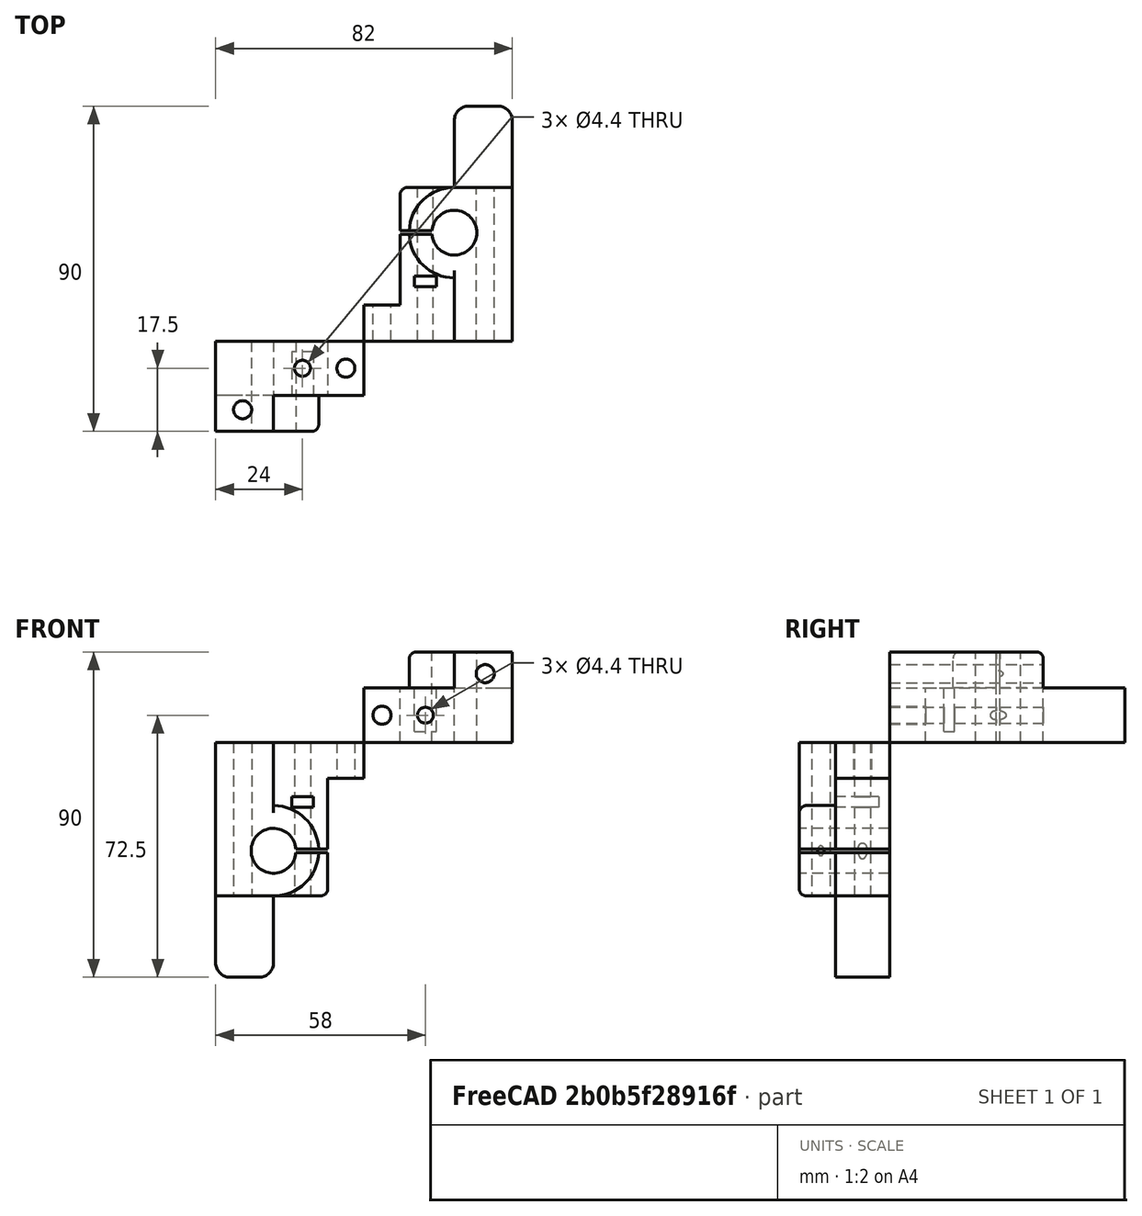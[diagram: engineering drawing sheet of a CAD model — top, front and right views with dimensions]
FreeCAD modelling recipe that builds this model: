
FCSTD DOCUMENT  (FreeCAD 0.15R4664 (Git))
Label: foot_L
License: All rights reserved
LicenseURL: http://en.wikipedia.org/wiki/All_rights_reserved
objects: Part::Box×6, Part::Cut×6, Part::Cylinder×5, Part::Fillet×4, Part::Feature×3, Part::MultiFuse×3, Mesh::Feature×1
note: 27 computed .brp shape members not serialized (recipe doc carries the construction recipe); baked Part::Feature solids carry a one-line shape summary decoded from their .brp

FEATURE [Mesh::Feature] footL_12mm
FEATURE [Part::Feature] footL_12mm001001  label="footL_12mm002"
  shape: bbox 41 x 65 x 25 mm, 3230 faces, 0 solids (baked)
FEATURE [Part::Box] Box  label="Cubo"
  Height = 15
  Length = 41
  Width = 65
FEATURE [Part::Box] Box001  label="Cubo001"
  Height = 10
  Length = 16
  Placement = pos=(25,0,15) rot=(0,0,1;0rad)
  Width = 42.5
FEATURE [Part::Cylinder] Cylinder  label="Cilindro"
  Angle = 360
  Height = 10
  Placement = pos=(25,30,15) rot=(0,0,1;0rad)
  Radius = 12.5
FEATURE [Part::Box] Box002  label="Cubo002"
  Height = 15
  Length = 10
  Placement = pos=(0,10,0) rot=(0,0,1;0rad)
  Width = 55
FEATURE [Part::Box] Box003  label="Cubo003"
  Height = 15
  Length = 15
  Placement = pos=(10,42.5,0) rot=(0,0,1;0rad)
  Width = 22.5
FEATURE [Part::Box] Box004  label="Cubo004"
  Height = 30
  Length = 25
  Placement = pos=(0,29.5,-2) rot=(0,0,1;0rad)
  Width = 1
FEATURE [Part::Box] Box005  label="Cubo005"
  Height = 17
  Length = 6
  Placement = pos=(14,15,3) rot=(0,0,1;0rad)
  Width = 3
FEATURE [Part::Cylinder] Cylinder001  label="Cilindro001"
  Angle = 360
  Height = 32
  Placement = pos=(25,30,-4) rot=(0,0,1;0rad)
  Radius = 6.2
FEATURE [Part::Cylinder] Cylinder002  label="Cilindro002"
  Angle = 360
  Height = 45
  Placement = pos=(33.55,-1,19) rot=(-1,0,0;1.5708rad)
  Radius = 2.5
FEATURE [Part::Cylinder] Cylinder003  label="Cilindro003"
  Angle = 360
  Height = 45
  Placement = pos=(17,-1,7.5) rot=(-1,0,0;1.5708rad)
  Radius = 2.2
FEATURE [Part::Cylinder] Cylinder004  label="Cilindro004"
  Angle = 360
  Height = 12
  Placement = pos=(5,-1,7.5) rot=(-1,0,0;1.5708rad)
  Radius = 2.5
FEATURE [Part::Cut] Cut
  Base = -> Box
  Tool = -> Box002
FEATURE [Part::MultiFuse] Fusion
  Shapes = -> [Cut,Box001]
FEATURE [Part::MultiFuse] Fusion001
  Shapes = -> [Fusion,Cylinder]
FEATURE [Part::Cut] Cut001
  Base = -> Fusion001
  Tool = -> Box003
FEATURE [Part::MultiFuse] Fusion002
  Shapes = -> [Cylinder004,Cylinder002,Cylinder003]
FEATURE [Part::Cut] Cut002
  Base = -> Cut001
  Tool = -> Fusion002
FEATURE [Part::Cut] Cut003
  Base = -> Cut002
  Tool = -> Cylinder001
FEATURE [Part::Cut] Cut004
  Base = -> Cut003
  Tool = -> Box005
FEATURE [Part::Cut] Cut005
  Base = -> Cut004
  Tool = -> Box004
FEATURE [Part::Fillet] Fillet
  Base = -> Cut005
  Edges = 1 edges r=2: [Edge35]
FEATURE [Part::Fillet] Fillet001
  Base = -> Fillet
  Edges = 1 edges r=2: [Edge9]
FEATURE [Part::Fillet] Fillet002
  Base = -> Fillet001
  Edges = 1 edges r=2: [Edge65]
FEATURE [Part::Fillet] Fillet003
  Base = -> Fillet002
  Edges = 2 edges r=4: [Edge51,Edge61]
FEATURE [Part::Feature] Fillet003_solid  label="Fillet003 (Solid)"
  shape: bbox 41 x 65 x 25 mm, 38 faces (baked)
FEATURE [Part::Feature] Fillet003_solid001  label="Fillet003 (Solid)001"
  Placement = pos=(0,0,0) rot=(0,0.707107,-0.707107;3.14159rad)
  shape: bbox 41 x 25 x 65 mm, 37 faces (baked)
